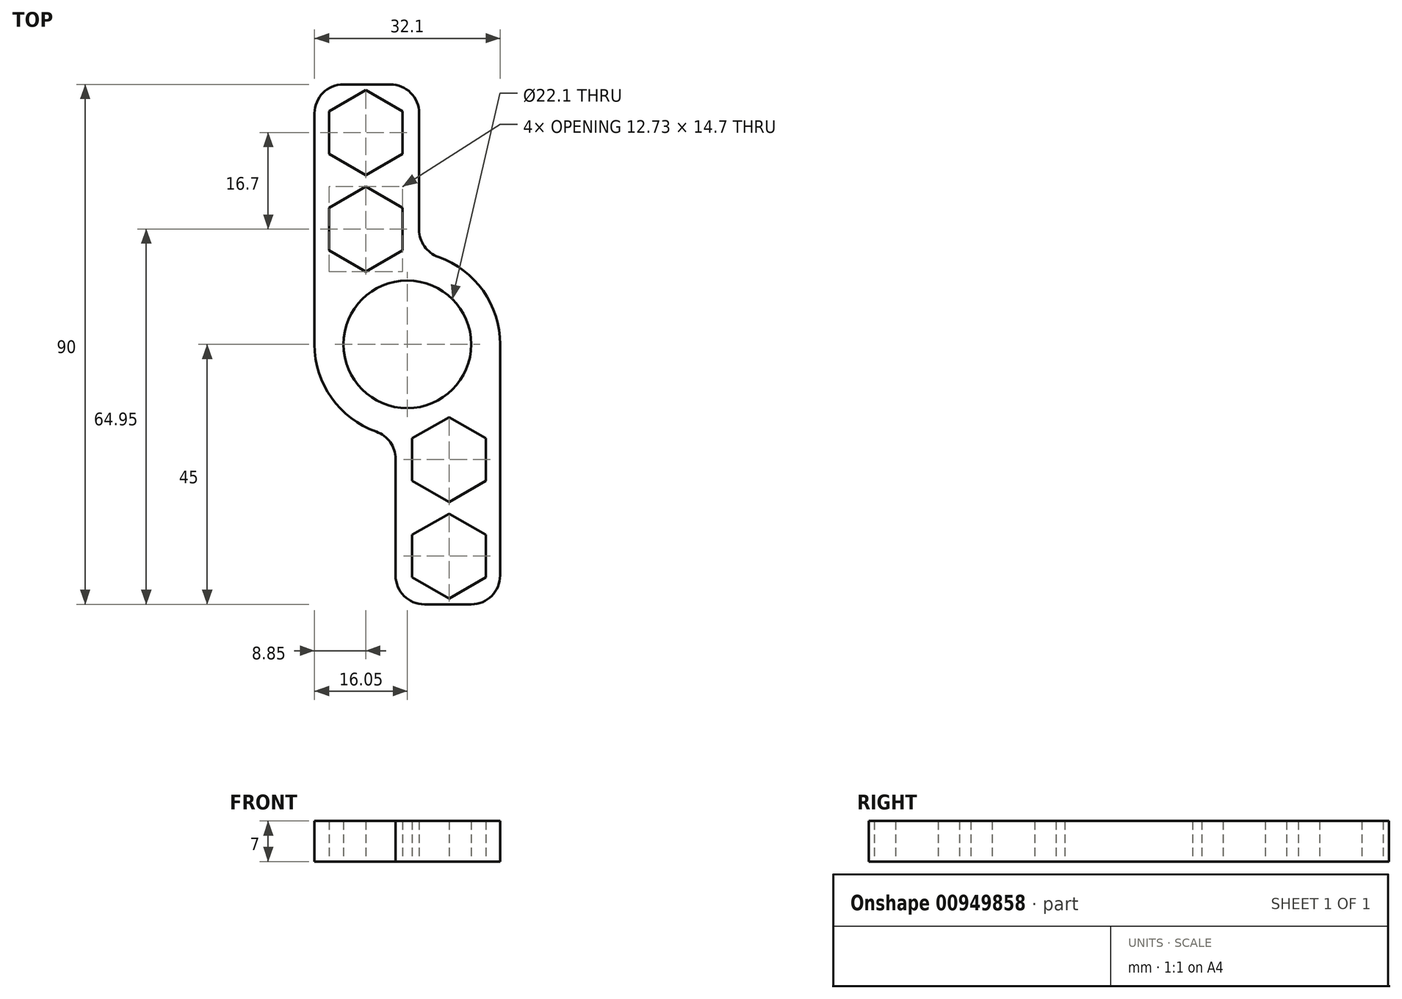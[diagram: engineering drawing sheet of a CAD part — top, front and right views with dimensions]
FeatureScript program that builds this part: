
annotation { "Feature Type Name" : "Feature", "Feature Type Description" : "" }
export const myFeature = defineFeature(function(context is Context, id is Id, definition is map)
    precondition{}
    {
        {
            var Q0;
            Q0=qCreatedBy(makeId("Top.planeOp"),FACE);
            var sketch = newSketch(context, id + "F0", { "sketchPlane" : qUnion([Q0])});
            skArc(sketch, "E0", {"start": v(11.05, 0) * mm, "mid": v(0, 11.05) * mm, "end": v(-11.05, 0) * mm});
            skArc(sketch, "E1.0", {"start": v(-8.72, 13.48) * mm, "mid": v(-9.1, 13.22) * mm, "end": v(-9.47, 12.96) * mm});
            skLineSegment(sketch, "E2", {"start": v(-16.05, 0) * mm, "end": v(-16.05, 40) * mm});
            skLineSegment(sketch, "E3", {"start": v(-11.05, 45) * mm, "end": v(-2.96, 45) * mm});
            skPoint(sketch, "E4", {"position": v(-7.2, 36.6) * mm});
            skPoint(sketch, "E4.positionSnap0", {"position": v(-7.2, 44) * mm});
            skCircle(sketch, "E5.cCircle", {"center": v(-7.2, 36.65) * mm, "radius": 7.35 * mm, "construction": true});
            skLineSegment(sketch, "E5.0", {"start": v(-7.2, 44) * mm, "end": v(-0.83, 40.33) * mm});
            skLineSegment(sketch, "E5.1", {"start": v(-0.83, 40.33) * mm, "end": v(-0.83, 32.98) * mm});
            skLineSegment(sketch, "E5.2", {"start": v(-0.83, 32.98) * mm, "end": v(-7.2, 29.3) * mm});
            skLineSegment(sketch, "E5.3", {"start": v(-7.2, 29.3) * mm, "end": v(-13.57, 32.98) * mm});
            skLineSegment(sketch, "E5.4", {"start": v(-13.57, 32.98) * mm, "end": v(-13.57, 40.33) * mm});
            skLineSegment(sketch, "E5.5", {"start": v(-13.57, 40.33) * mm, "end": v(-7.2, 44) * mm});
            skCircle(sketch, "E6.cCircle", {"center": v(-7.2, 19.95) * mm, "radius": 7.35 * mm, "construction": true});
            skLineSegment(sketch, "E6.0", {"start": v(-7.2, 27.3) * mm, "end": v(-0.83, 23.63) * mm});
            skLineSegment(sketch, "E6.1", {"start": v(-0.83, 23.63) * mm, "end": v(-0.83, 16.28) * mm});
            skLineSegment(sketch, "E6.2", {"start": v(-0.83, 16.28) * mm, "end": v(-7.2, 12.6) * mm});
            skLineSegment(sketch, "E6.3", {"start": v(-7.2, 12.6) * mm, "end": v(-13.57, 16.28) * mm});
            skLineSegment(sketch, "E6.4", {"start": v(-13.57, 16.28) * mm, "end": v(-13.57, 23.63) * mm});
            skLineSegment(sketch, "E6.5", {"start": v(-13.57, 23.63) * mm, "end": v(-7.2, 27.3) * mm});
            skPoint(sketch, "E7.visualSharp", {"position": v(2.04, 15.92) * mm});
            skPoint(sketch, "E8.visualSharp", {"position": v(-16.05, 45) * mm});
            skArc(sketch, "E8.filletArc", {"start": v(-11.05, 45) * mm, "mid": v(-14.59, 43.54) * mm, "end": v(-16.05, 40) * mm});
            skPoint(sketch, "E9.visualSharp", {"position": v(3.49, 45) * mm});
            skArc(sketch, "E9.filletArc", {"start": v(2.04, 40) * mm, "mid": v(0.57, 43.54) * mm, "end": v(-2.96, 45) * mm});
            skArc(sketch, "E10", {"start": v(-11.05, 0) * mm, "mid": v(0, -11.05) * mm, "end": v(11.05, 0) * mm});
            skArc(sketch, "E11.0", {"start": v(8.72, -13.48) * mm, "mid": v(9.1, -13.22) * mm, "end": v(9.47, -12.96) * mm});
            skLineSegment(sketch, "E12", {"start": v(16.05, 0) * mm, "end": v(16.05, -40) * mm});
            skLineSegment(sketch, "E13", {"start": v(11.05, -45) * mm, "end": v(2.96, -45) * mm});
            skPoint(sketch, "E14", {"position": v(7.2, -36.65) * mm});
            skPoint(sketch, "E14.positionSnap0", {"position": v(7.2, -44) * mm});
            skCircle(sketch, "E15.cCircle", {"center": v(7.2, -36.65) * mm, "radius": 7.35 * mm, "construction": true});
            skLineSegment(sketch, "E15.0", {"start": v(7.2, -44) * mm, "end": v(0.83, -40.33) * mm});
            skLineSegment(sketch, "E15.1", {"start": v(0.83, -40.33) * mm, "end": v(0.83, -32.98) * mm});
            skLineSegment(sketch, "E15.2", {"start": v(0.83, -32.98) * mm, "end": v(7.2, -29.3) * mm});
            skLineSegment(sketch, "E15.3", {"start": v(7.2, -29.3) * mm, "end": v(13.57, -32.97) * mm});
            skLineSegment(sketch, "E15.4", {"start": v(13.57, -32.97) * mm, "end": v(13.57, -40.33) * mm});
            skLineSegment(sketch, "E15.5", {"start": v(13.57, -40.32) * mm, "end": v(7.2, -44) * mm});
            skCircle(sketch, "E16.cCircle", {"center": v(7.2, -19.95) * mm, "radius": 7.35 * mm, "construction": true});
            skLineSegment(sketch, "E16.0", {"start": v(7.2, -27.3) * mm, "end": v(0.83, -23.63) * mm});
            skLineSegment(sketch, "E16.1", {"start": v(0.83, -23.62) * mm, "end": v(0.83, -16.28) * mm});
            skLineSegment(sketch, "E16.2", {"start": v(0.83, -16.28) * mm, "end": v(7.2, -12.6) * mm});
            skLineSegment(sketch, "E16.3", {"start": v(7.2, -12.6) * mm, "end": v(13.57, -16.28) * mm});
            skLineSegment(sketch, "E16.4", {"start": v(13.57, -16.28) * mm, "end": v(13.57, -23.63) * mm});
            skLineSegment(sketch, "E16.5", {"start": v(13.57, -23.63) * mm, "end": v(7.2, -27.3) * mm});
            skPoint(sketch, "E17.visualSharp", {"position": v(-2.04, -15.92) * mm});
            skPoint(sketch, "E18.visualSharp", {"position": v(16.05, -45) * mm});
            skArc(sketch, "E18.filletArc", {"start": v(11.05, -45) * mm, "mid": v(14.59, -43.54) * mm, "end": v(16.05, -40) * mm});
            skPoint(sketch, "E19.visualSharp", {"position": v(-3.49, -45) * mm});
            skArc(sketch, "E19.filletArc", {"start": v(-2.04, -40) * mm, "mid": v(-0.57, -43.54) * mm, "end": v(2.96, -45) * mm});
            skLineSegment(sketch, "E20", {"start": v(2.04, 40) * mm, "end": v(2.04, 19.84) * mm});
            skLineSegment(sketch, "E21", {"start": v(-2.04, -40) * mm, "end": v(-2.04, -19.84) * mm});
            skArc(sketch, "E22", {"start": v(5.37, 15.13) * mm, "mid": v(13.1, 9.26) * mm, "end": v(16.05, 0) * mm});
            skArc(sketch, "E23", {"start": v(-16.05, 0) * mm, "mid": v(-13.1, -9.26) * mm, "end": v(-5.37, -15.13) * mm});
            skArc(sketch, "E24.filletArc", {"start": v(2.04, 19.84) * mm, "mid": v(2.95, 16.95) * mm, "end": v(5.37, 15.13) * mm});
            skArc(sketch, "E25.filletArc", {"start": v(-2.04, -19.84) * mm, "mid": v(-2.95, -16.95) * mm, "end": v(-5.37, -15.13) * mm});
            skSolve(sketch);
        }
        {
            var Q0;
            Q0=makeQuery(id+"F0.imprint","IMPRINT",FACE,{"disambiguationData":[TD([[makeQuery(id+"F0.imprint","IMPRINT",EDGE,{"derivedFrom":sQuery(id+"F0.wireOp",EDGE,"E0")}),-1.0]])]});
            extrude(context, id + "F1", {"entities" : qUnion([Q0]), "depth" : 7 * mm, "offsetDistance" : 25 * mm});
        }
    });
